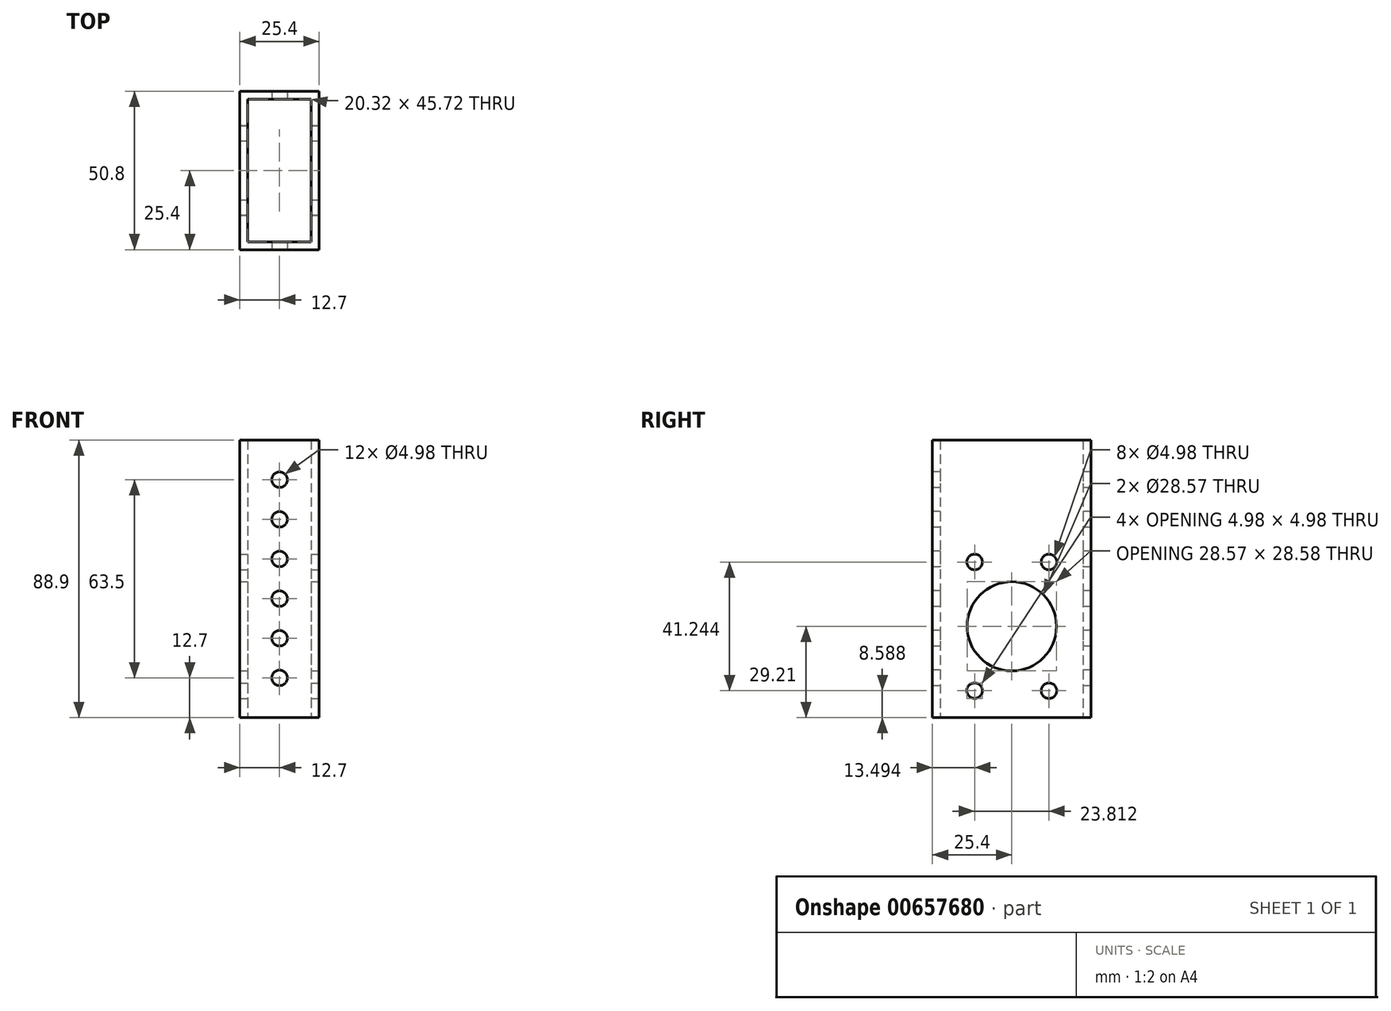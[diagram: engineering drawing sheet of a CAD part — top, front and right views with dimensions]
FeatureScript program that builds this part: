
annotation { "Feature Type Name" : "Feature", "Feature Type Description" : "" }
export const myFeature = defineFeature(function(context is Context, id is Id, definition is map)
    precondition{}
    {
        {
            var Q0;
            Q0=qCreatedBy(makeId("Top.planeOp"),FACE);
            var sketch = newSketch(context, id + "F0", { "sketchPlane" : qUnion([Q0])});
            skLineSegment(sketch, "E0.bottom", {"start": v(0, 0) * mm, "end": v(25.4, 0) * mm});
            skLineSegment(sketch, "E0.top", {"start": v(0, -50.8) * mm, "end": v(25.4, -50.8) * mm});
            skLineSegment(sketch, "E0.left", {"start": v(0, 0) * mm, "end": v(0, -50.8) * mm});
            skLineSegment(sketch, "E0.right", {"start": v(25.4, 0) * mm, "end": v(25.4, -50.8) * mm});
            skLineSegment(sketch, "E1.bottom", {"start": v(2.54, -48.26) * mm, "end": v(22.86, -48.26) * mm});
            skLineSegment(sketch, "E1.top", {"start": v(2.54, -2.54) * mm, "end": v(22.86, -2.54) * mm});
            skLineSegment(sketch, "E1.left", {"start": v(2.54, -48.26) * mm, "end": v(2.54, -2.54) * mm});
            skLineSegment(sketch, "E1.right", {"start": v(22.86, -48.26) * mm, "end": v(22.86, -2.54) * mm});
            skSolve(sketch);
        }
        {
            var Q0;
            Q0=makeQuery(id+"F0.imprint","IMPRINT",FACE,{"disambiguationData":[TD([[makeQuery(id+"F0.imprint","IMPRINT",EDGE,{"derivedFrom":sQuery(id+"F0.wireOp",EDGE,"E0.bottom")}),-1.0]])]});
            extrude(context, id + "F1", {"entities" : qUnion([Q0]), "depth" : 88.9 * mm, "offsetDistance" : 25.4 * mm});
        }
        {
            var Q0;
            Q0=makeQuery(id+"F1.opExtrude","SWEPT_FACE",FACE,{"disambiguationData":[OSD([sQuery(id+"F0.wireOp",EDGE,"E0.right")])]});
            var sketch = newSketch(context, id + "F2", { "sketchPlane" : qUnion([Q0])});
            skCircle(sketch, "E2", {"center": v(-25.4, 29.21) * mm, "radius": 14.29 * mm});
            skLineSegment(sketch, "E3.direction1", {"start": v(-25.4, 12.7) * mm, "end": v(0, 12.7) * mm, "construction": true});
            skLineSegment(sketch, "E3.direction2", {"start": v(-25.4, 12.7) * mm, "end": v(-25.4, 38.1) * mm, "construction": true});
            skSolve(sketch);
        }
        {
            var Q0;
            Q0=makeQuery(id+"F2.imprint","IMPRINT",FACE,{"disambiguationData":[TD([[makeQuery(id+"F2.imprint","IMPRINT",EDGE,{"derivedFrom":sQuery(id+"F2.wireOp",EDGE,"E2")}),1.0]])]});
            var Q1;
            Q1=makeQuery(id+"F2.imprint","IMPRINT",FACE,{"disambiguationData":[TD([[makeQuery(id+"F2.imprint","IMPRINT",EDGE,{"derivedFrom":sQuery(id+"F2.wireOp",EDGE,"E3.0.3.0")}),1.0]])]});
            var Q2;
            Q2=makeQuery(id+"F2.imprint","IMPRINT",FACE,{"disambiguationData":[TD([[makeQuery(id+"F2.imprint","IMPRINT",EDGE,{"derivedFrom":sQuery(id+"F2.wireOp",EDGE,"E3.0.2.0")}),1.0]])]});
            var Q3;
            Q3=makeQuery(id+"F2.imprint","IMPRINT",FACE,{"disambiguationData":[TD([[makeQuery(id+"F2.imprint","IMPRINT",EDGE,{"derivedFrom":sQuery(id+"F2.wireOp",EDGE,"E3.0.1.0")}),1.0]])]});
            var Q4;
            Q4=makeQuery(id+"F2.imprint","IMPRINT",FACE,{"disambiguationData":[TD([[makeQuery(id+"F2.imprint","IMPRINT",EDGE,{"derivedFrom":sQuery(id+"F2.wireOp",EDGE,"cuAgHkHt-oJ07-7mtN-8Eyz-TgJwgslHKFw5")}),1.0]])]});
            extrude(context, id + "F3", {"entities" : qUnion([Q0, Q1, Q2, Q3, Q4]), "operationType" : NewBodyOperationType.REMOVE, "oppositeDirection" : true, "depth" : 50.8 * mm, "offsetDistance" : 25.4 * mm});
        }
        {
            var Q0;
            Q0=makeQuery(id+"F1.opExtrude","SWEPT_FACE",FACE,{"disambiguationData":[OSD([sQuery(id+"F0.wireOp",EDGE,"E0.right")])]});
            var sketch = newSketch(context, id + "F4", { "sketchPlane" : qUnion([Q0])});
            skCircle(sketch, "E4", {"center": v(-25.4, 29.21) * mm, "radius": 23.81 * mm, "construction": true});
            skCircle(sketch, "E5", {"center": v(-13.5, 49.83) * mm, "radius": 2.49 * mm});
            skCircle(sketch, "E6.1.0", {"center": v(-1.59, 29.21) * mm, "radius": 2.49 * mm, "construction": true});
            skCircle(sketch, "E6.2.0", {"center": v(-13.5, 8.59) * mm, "radius": 2.49 * mm});
            skCircle(sketch, "E6.3.0", {"center": v(-37.3, 8.59) * mm, "radius": 2.49 * mm});
            skCircle(sketch, "E6.4.0", {"center": v(-49.21, 29.21) * mm, "radius": 2.49 * mm, "construction": true});
            skCircle(sketch, "E6.5.0", {"center": v(-37.3, 49.83) * mm, "radius": 2.49 * mm});
            skLineSegment(sketch, "E6.anchor1", {"start": v(-25.4, 29.21) * mm, "end": v(-13.5, 49.83) * mm, "construction": true});
            skLineSegment(sketch, "E6.anchor2", {"start": v(-25.4, 29.21) * mm, "end": v(-37.3, 49.83) * mm, "construction": true});
            skSolve(sketch);
        }
        {
            var Q0;
            Q0 = qSketchRegion(id + "F4", true);
            extrude(context, id + "F5", {"entities" : qUnion([Q0]), "operationType" : NewBodyOperationType.REMOVE, "endBound" : BoundingType.THROUGH_ALL, "oppositeDirection" : true, "depth" : 25.4 * mm, "offsetDistance" : 25.4 * mm});
        }
        {
            var Q0;
            Q0=makeQuery(id+"F1.opExtrude","SWEPT_FACE",FACE,{"disambiguationData":[OSD([sQuery(id+"F0.wireOp",EDGE,"E0.top")])]});
            var sketch = newSketch(context, id + "F6", { "sketchPlane" : qUnion([Q0])});
            skCircle(sketch, "E7", {"center": v(12.7, 12.7) * mm, "radius": 2.49 * mm});
            skCircle(sketch, "E8.0.1.0", {"center": v(12.7, 25.4) * mm, "radius": 2.49 * mm});
            skCircle(sketch, "E8.0.2.0", {"center": v(12.7, 38.1) * mm, "radius": 2.49 * mm});
            skCircle(sketch, "E8.0.3.0", {"center": v(12.7, 50.8) * mm, "radius": 2.49 * mm});
            skCircle(sketch, "E8.0.4.0", {"center": v(12.7, 63.5) * mm, "radius": 2.49 * mm});
            skCircle(sketch, "E8.0.5.0", {"center": v(12.7, 76.2) * mm, "radius": 2.49 * mm});
            skLineSegment(sketch, "E8.direction1", {"start": v(12.7, 12.7) * mm, "end": v(38.1, 12.7) * mm, "construction": true});
            skLineSegment(sketch, "E8.direction2", {"start": v(12.7, 12.7) * mm, "end": v(12.7, 25.4) * mm, "construction": true});
            skSolve(sketch);
        }
        {
            var Q0;
            Q0 = qSketchRegion(id + "F6", true);
            extrude(context, id + "F7", {"entities" : qUnion([Q0]), "operationType" : NewBodyOperationType.REMOVE, "endBound" : BoundingType.THROUGH_ALL, "oppositeDirection" : true, "depth" : 25.4 * mm, "offsetDistance" : 25.4 * mm});
        }
    });
